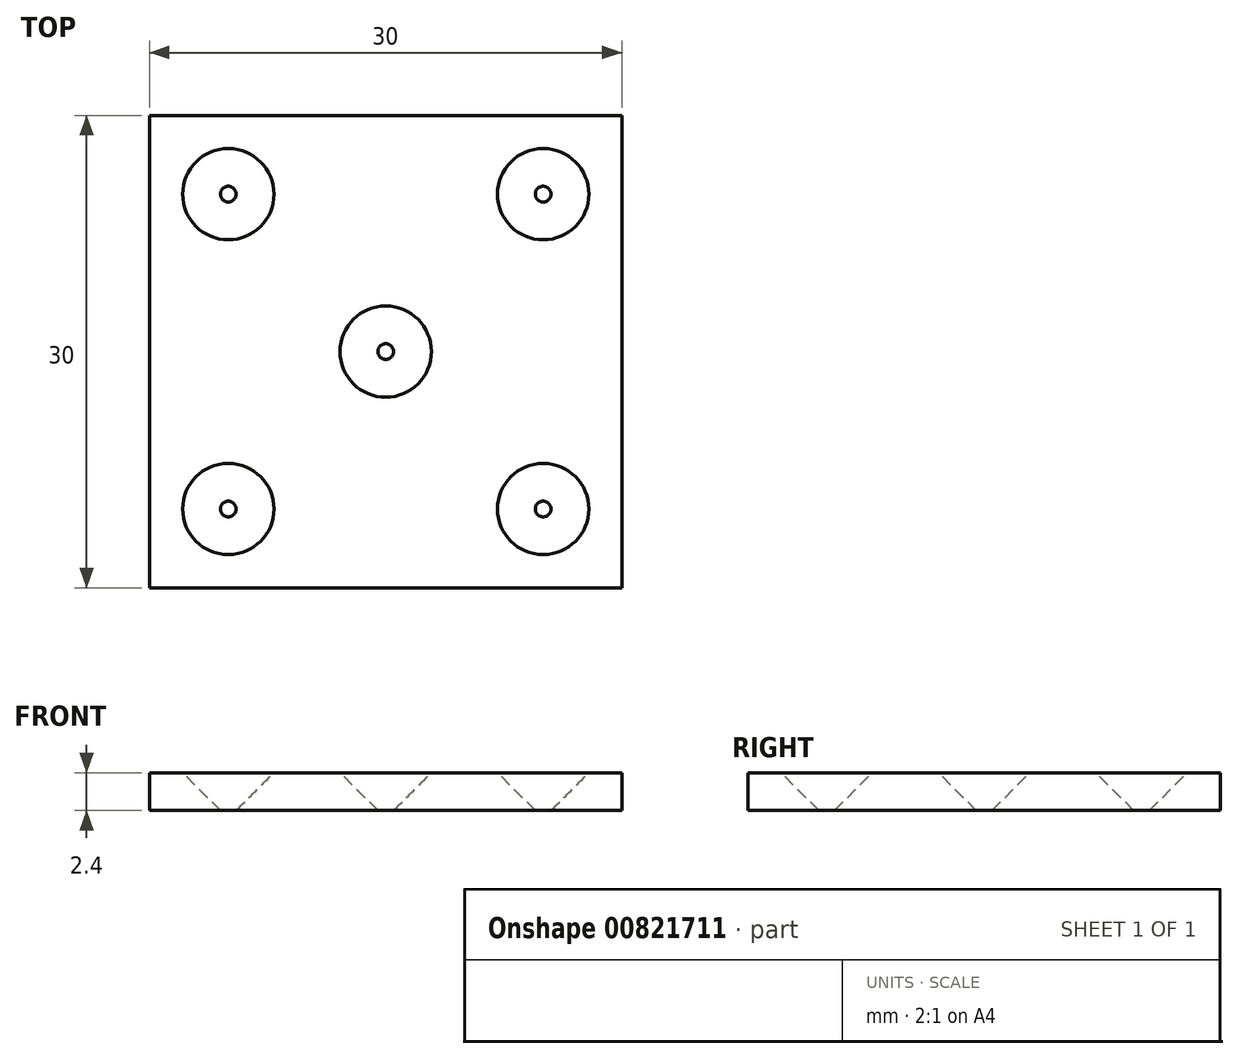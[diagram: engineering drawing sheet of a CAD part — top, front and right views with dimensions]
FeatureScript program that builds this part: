
annotation { "Feature Type Name" : "Feature", "Feature Type Description" : "" }
export const myFeature = defineFeature(function(context is Context, id is Id, definition is map)
    precondition{}
    {
        {
            var Q0;
            Q0=qCreatedBy(makeId("Top.planeOp"),FACE);
            var sketch = newSketch(context, id + "F0", { "sketchPlane" : qUnion([Q0])});
            skLineSegment(sketch, "E0.bottom", {"start": v(-15, 15) * mm, "end": v(15, 15) * mm});
            skLineSegment(sketch, "E0.top", {"start": v(-15, -15) * mm, "end": v(15, -15) * mm});
            skLineSegment(sketch, "E0.left", {"start": v(-15, 15) * mm, "end": v(-15, -15) * mm});
            skLineSegment(sketch, "E0.right", {"start": v(15, 15) * mm, "end": v(15, -15) * mm});
            skPoint(sketch, "E0.middle", {"position": v(0, 0) * mm});
            skCircle(sketch, "E1", {"center": v(-10, 10) * mm, "radius": 0.4 * mm});
            skCircle(sketch, "E2.MirrorC", {"center": v(10, 10) * mm, "radius": 0.4 * mm});
            skCircle(sketch, "E3.MirrorC", {"center": v(10, -10) * mm, "radius": 0.4 * mm});
            skCircle(sketch, "E4.MirrorC", {"center": v(-10, -10) * mm, "radius": 0.4 * mm});
            skCircle(sketch, "E5", {"center": v(0, 0) * mm, "radius": 0.4 * mm});
            skSolve(sketch);
        }
        {
            var Q0;
            Q0=qSketchRegion(id+"F0",true);
            extrude(context, id + "F1", {"entities" : qUnion([Q0]), "depth" : 2.4 * mm, "offsetDistance" : 25 * mm});
        }
        {
            var Q0;
            Q0=makeQuery(id+"F1.opExtrude","CAP_EDGE",EDGE,{"disambiguationData":[OSD([sQuery(id+"F0.wireOp",EDGE,"E1")])],"isStart":false});
            var Q1;
            Q1=makeQuery(id+"F1.opExtrude","CAP_EDGE",EDGE,{"disambiguationData":[OSD([sQuery(id+"F0.wireOp",EDGE,"E2.MirrorC")])],"isStart":false});
            var Q2;
            Q2=makeQuery(id+"F1.opExtrude","CAP_EDGE",EDGE,{"disambiguationData":[OSD([sQuery(id+"F0.wireOp",EDGE,"E3.MirrorC")])],"isStart":false});
            var Q3;
            Q3=makeQuery(id+"F1.opExtrude","CAP_EDGE",EDGE,{"disambiguationData":[OSD([sQuery(id+"F0.wireOp",EDGE,"E4.MirrorC")])],"isStart":false});
            var Q4;
            Q4=makeQuery(id+"F1.opExtrude","CAP_EDGE",EDGE,{"disambiguationData":[OSD([sQuery(id+"F0.wireOp",EDGE,"E5")])],"isStart":false});
            chamfer(context, id + "F2", {"entities" : qUnion([Q0, Q1, Q2, Q3, Q4]), "width" : 2.5 * mm, "tangentPropagation" : true});
        }
    });
